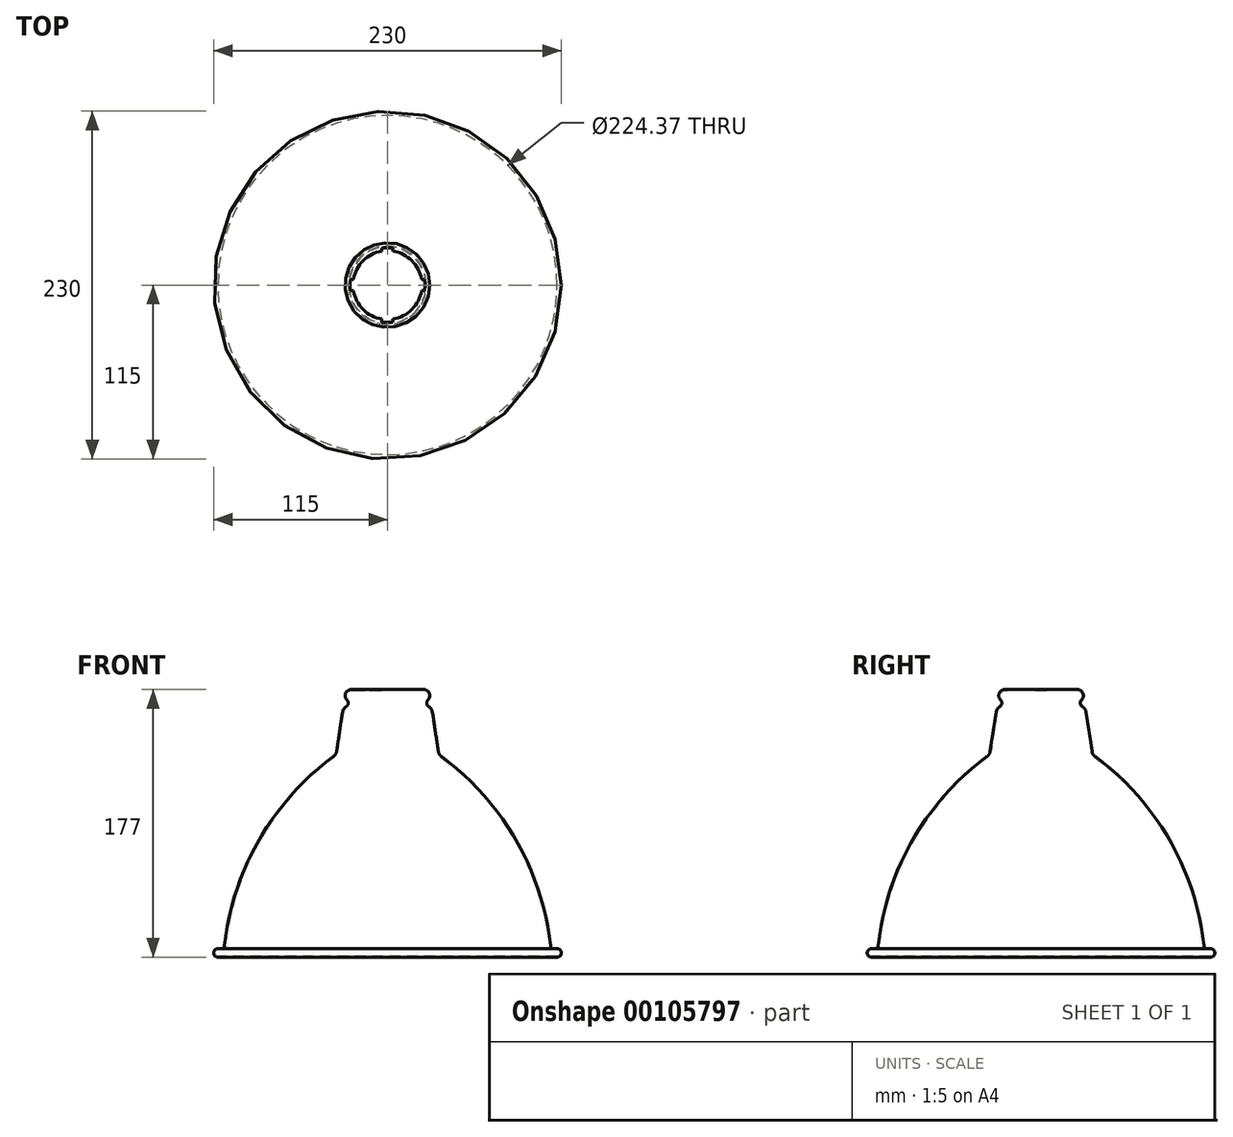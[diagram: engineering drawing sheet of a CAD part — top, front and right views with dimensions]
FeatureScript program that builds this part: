
annotation { "Feature Type Name" : "Feature", "Feature Type Description" : "" }
export const myFeature = defineFeature(function(context is Context, id is Id, definition is map)
    precondition{}
    {
        {
            var Q0;
            Q0=qCreatedBy(makeId("Right.planeOp"),FACE);
            var sketch = newSketch(context, id + "F0", { "sketchPlane" : qUnion([Q0])});
            skLineSegment(sketch, "E0", {"start": v(0, 47.08) * mm, "end": v(0, -149.22) * mm, "construction": true});
            skLineSegment(sketch, "E1", {"start": v(23.94, 47.68) * mm, "end": v(23.94, -145.08) * mm, "construction": true});
            skArc(sketch, "E2", {"start": v(26.81, 37.57) * mm, "mid": v(27.69, 42) * mm, "end": v(23.94, 44.5) * mm});
            skArc(sketch, "E3", {"start": v(26.81, 37.57) * mm, "mid": v(26.02, 35.27) * mm, "end": v(27.34, 33.22) * mm});
            skLineSegment(sketch, "E4", {"start": v(27.15, 46.34) * mm, "end": v(29.2, 32.85) * mm, "construction": true});
            skLineSegment(sketch, "E5", {"start": v(29.69, 29.7) * mm, "end": v(33.69, 3.56) * mm});
            skPoint(sketch, "E6.visualSharp", {"position": v(29.2, 32.85) * mm});
            skArc(sketch, "E6.filletArc", {"start": v(29.69, 29.7) * mm, "mid": v(28.9, 31.73) * mm, "end": v(27.34, 33.22) * mm});
            skPoint(sketch, "E7.visualSharp", {"position": v(34, 1.5) * mm});
            skArc(sketch, "E8", {"start": v(112.19, -132.5) * mm, "mid": v(115, -129.68) * mm, "end": v(112.19, -126.87) * mm});
            skLineSegment(sketch, "E9", {"start": v(112.19, -126.87) * mm, "end": v(109.8, -126.87) * mm});
            skArc(sketch, "E10", {"start": v(107.81, -125.09) * mm, "mid": v(84.89, -54.83) * mm, "end": v(35.66, 0.3) * mm});
            skArc(sketch, "E11.filletArc", {"start": v(33.69, 3.56) * mm, "mid": v(34.35, 1.73) * mm, "end": v(35.66, 0.3) * mm});
            skLineSegment(sketch, "E12", {"start": v(115, -129.68) * mm, "end": v(115, -122.65) * mm, "construction": true});
            skPoint(sketch, "E13.visualSharp", {"position": v(108, -126.87) * mm});
            skArc(sketch, "E13.filletArc", {"start": v(107.81, -125.09) * mm, "mid": v(108.47, -126.36) * mm, "end": v(109.8, -126.87) * mm});
            skArc(sketch, "E14.0", {"start": v(26.46, 37.92) * mm, "mid": v(27.23, 41.8) * mm, "end": v(23.94, 44) * mm});
            skArc(sketch, "E14.1", {"start": v(26.46, 37.92) * mm, "mid": v(25.53, 35.21) * mm, "end": v(27.08, 32.8) * mm});
            skArc(sketch, "E14.2", {"start": v(29.2, 29.63) * mm, "mid": v(28.5, 31.45) * mm, "end": v(27.08, 32.8) * mm});
            skLineSegment(sketch, "E14.3", {"start": v(29.2, 29.63) * mm, "end": v(33.2, 3.49) * mm});
            skArc(sketch, "E14.4", {"start": v(33.2, 3.49) * mm, "mid": v(33.92, 1.48) * mm, "end": v(35.37, -0.1) * mm});
            skArc(sketch, "E14.5", {"start": v(112.19, -132) * mm, "mid": v(114.5, -129.68) * mm, "end": v(112.19, -127.37) * mm});
            skLineSegment(sketch, "E14.6", {"start": v(112.19, -127.37) * mm, "end": v(109.8, -127.37) * mm});
            skArc(sketch, "E14.7", {"start": v(107.32, -125.14) * mm, "mid": v(108.14, -126.73) * mm, "end": v(109.8, -127.37) * mm});
            skArc(sketch, "E14.8", {"start": v(107.32, -125.14) * mm, "mid": v(84.46, -55.08) * mm, "end": v(35.37, -0.1) * mm});
            skLineSegment(sketch, "E15", {"start": v(23.94, 44.5) * mm, "end": v(23.94, 44) * mm});
            skLineSegment(sketch, "E16", {"start": v(112.19, -132) * mm, "end": v(112.19, -132.5) * mm});
            skLineSegment(sketch, "E17", {"start": v(23.94, 44.5) * mm, "end": v(22.8, 44.5) * mm});
            skLineSegment(sketch, "E18", {"start": v(23.94, 44) * mm, "end": v(22.8, 44) * mm});
            skLineSegment(sketch, "E19", {"start": v(22.8, 44) * mm, "end": v(22.8, 44.5) * mm});
            skSolve(sketch);
        }
        {
            var Q0;
            Q0=makeQuery(id+"F0.imprint","IMPRINT",FACE,{"disambiguationData":[TD([[makeQuery(id+"F0.imprint","IMPRINT",EDGE,{"derivedFrom":sQuery(id+"F0.wireOp",EDGE,"E2")}),1.0]])]});
            var Q1;
            Q1=makeQuery(id+"F0.imprint","IMPRINT",FACE,{"disambiguationData":[TD([[makeQuery(id+"F0.imprint","IMPRINT",EDGE,{"derivedFrom":sQuery(id+"F0.wireOp",EDGE,"E15")}),-1.0]])]});
            var Q2;
            Q2=sQuery(id+"F0.wireOp",EDGE,"E0");
            revolve(context, id + "F1", {"entities" : qUnion([Q0, Q1]), "axis" : qUnion([Q2]), "revolveType" : RevolveType.FULL});
        }
        {
            var Q0;
            Q0=makeQuery(id+"F1.opRevolve","SWEPT_FACE",FACE,{"disambiguationData":[OSD([sQuery(id+"F0.wireOp",EDGE,"E17")])]});
            var sketch = newSketch(context, id + "F2", { "sketchPlane" : qUnion([Q0])});
            skLineSegment(sketch, "E20", {"start": v(0, 25.62) * mm, "end": v(0, -27.1) * mm, "construction": true});
            skLineSegment(sketch, "E21", {"start": v(-26.7, 0) * mm, "end": v(26.56, 0) * mm, "construction": true});
            skLineSegment(sketch, "E22", {"start": v(-18.35, 18.35) * mm, "end": v(18.35, -18.35) * mm, "construction": true});
            skCircle(sketch, "E23", {"center": v(0, 0) * mm, "radius": 24.72 * mm});
            skLineSegment(sketch, "E24", {"start": v(-3.65, 22.5) * mm, "end": v(-3.65, 24.45) * mm});
            skLineSegment(sketch, "E25.MirrorCS", {"start": v(3.65, 22.5) * mm, "end": v(3.65, 24.45) * mm});
            skLineSegment(sketch, "E26.MirrorCS", {"start": v(-3.65, -22.5) * mm, "end": v(-3.65, -24.45) * mm});
            skLineSegment(sketch, "E27.MirrorCS", {"start": v(3.65, -22.5) * mm, "end": v(3.65, -24.45) * mm});
            skLineSegment(sketch, "E28.MirrorCS", {"start": v(-22.5, 3.65) * mm, "end": v(-24.45, 3.65) * mm});
            skLineSegment(sketch, "E29.MirrorCS", {"start": v(-22.5, -3.65) * mm, "end": v(-24.45, -3.65) * mm});
            skLineSegment(sketch, "E30.MirrorCS", {"start": v(22.5, -3.65) * mm, "end": v(24.45, -3.65) * mm});
            skLineSegment(sketch, "E31.MirrorCS", {"start": v(22.5, 3.65) * mm, "end": v(24.45, 3.65) * mm});
            skSolve(sketch);
        }
        {
            var Q0;
            {var subQ0=sQuery(id+"F2.wireOp",EDGE,"E28.MirrorCS");var subQ1=sQuery(id+"F0.wireOp",EDGE,"E17");var subQ2=makeQuery(id+"F1.opRevolve","SWEPT_EDGE",EDGE,{"disambiguationData":[OSD([subQ1,sQuery(id+"F0.wireOp",EDGE,"E19")])]});var subQ3=makeQuery(id+"F2.imprint","INTERSECT",VERTEX,{"derivedFrom":[subQ2,subQ0]});Q0=makeQuery(id+"F2.imprint","IMPRINT",FACE,{"disambiguationData":[TD([[makeQuery(id+"F2.imprint","IMPRINT",EDGE,{"disambiguationData":[TD([[subQ3,-1.0]])],"derivedFrom":subQ0}),1.0]])]});}
            var Q1;
            {var subQ0=sQuery(id+"F2.wireOp",EDGE,"E28.MirrorCS");var subQ1=sQuery(id+"F2.wireOp",EDGE,"E23");var subQ2=makeQuery(id+"F2.imprint","INTERSECT",VERTEX,{"derivedFrom":[subQ1,subQ0]});Q1=makeQuery(id+"F2.imprint","IMPRINT",FACE,{"disambiguationData":[TD([[makeQuery(id+"F2.imprint","IMPRINT",EDGE,{"disambiguationData":[TD([[subQ2,-1.0]])],"derivedFrom":subQ1}),1.0]])]});}
            var Q2;
            {var subQ0=sQuery(id+"F2.wireOp",EDGE,"E24");var subQ1=sQuery(id+"F0.wireOp",EDGE,"E17");var subQ2=makeQuery(id+"F1.opRevolve","SWEPT_EDGE",EDGE,{"disambiguationData":[OSD([subQ1,sQuery(id+"F0.wireOp",EDGE,"E19")])]});var subQ3=makeQuery(id+"F2.imprint","INTERSECT",VERTEX,{"derivedFrom":[subQ2,subQ0]});Q2=makeQuery(id+"F2.imprint","IMPRINT",FACE,{"disambiguationData":[TD([[makeQuery(id+"F2.imprint","IMPRINT",EDGE,{"disambiguationData":[TD([[subQ3,-1.0]])],"derivedFrom":subQ0}),-1.0]])]});}
            var Q3;
            {var subQ0=sQuery(id+"F2.wireOp",EDGE,"E24");var subQ1=sQuery(id+"F2.wireOp",EDGE,"E23");var subQ2=makeQuery(id+"F2.imprint","INTERSECT",VERTEX,{"derivedFrom":[subQ1,subQ0]});Q3=makeQuery(id+"F2.imprint","IMPRINT",FACE,{"disambiguationData":[TD([[makeQuery(id+"F2.imprint","IMPRINT",EDGE,{"disambiguationData":[TD([[subQ2,1.0]])],"derivedFrom":subQ1}),1.0]])]});}
            var Q4;
            {var subQ0=sQuery(id+"F2.wireOp",EDGE,"E30.MirrorCS");var subQ1=sQuery(id+"F0.wireOp",EDGE,"E17");var subQ2=makeQuery(id+"F1.opRevolve","SWEPT_EDGE",EDGE,{"disambiguationData":[OSD([subQ1,sQuery(id+"F0.wireOp",EDGE,"E19")])]});var subQ3=makeQuery(id+"F2.imprint","INTERSECT",VERTEX,{"derivedFrom":[subQ2,subQ0]});Q4=makeQuery(id+"F2.imprint","IMPRINT",FACE,{"disambiguationData":[TD([[makeQuery(id+"F2.imprint","IMPRINT",EDGE,{"disambiguationData":[TD([[subQ3,-1.0]])],"derivedFrom":subQ0}),1.0]])]});}
            var Q5;
            {var subQ0=sQuery(id+"F2.wireOp",EDGE,"E30.MirrorCS");var subQ1=sQuery(id+"F2.wireOp",EDGE,"E23");var subQ2=makeQuery(id+"F2.imprint","INTERSECT",VERTEX,{"derivedFrom":[subQ1,subQ0]});Q5=makeQuery(id+"F2.imprint","IMPRINT",FACE,{"disambiguationData":[TD([[makeQuery(id+"F2.imprint","IMPRINT",EDGE,{"disambiguationData":[TD([[subQ2,-1.0]])],"derivedFrom":subQ1}),1.0]])]});}
            var Q6;
            {var subQ0=sQuery(id+"F2.wireOp",EDGE,"E26.MirrorCS");var subQ1=sQuery(id+"F0.wireOp",EDGE,"E17");var subQ2=makeQuery(id+"F1.opRevolve","SWEPT_EDGE",EDGE,{"disambiguationData":[OSD([subQ1,sQuery(id+"F0.wireOp",EDGE,"E19")])]});var subQ3=makeQuery(id+"F2.imprint","INTERSECT",VERTEX,{"derivedFrom":[subQ2,subQ0]});Q6=makeQuery(id+"F2.imprint","IMPRINT",FACE,{"disambiguationData":[TD([[makeQuery(id+"F2.imprint","IMPRINT",EDGE,{"disambiguationData":[TD([[subQ3,-1.0]])],"derivedFrom":subQ0}),1.0]])]});}
            var Q7;
            {var subQ0=sQuery(id+"F2.wireOp",EDGE,"E26.MirrorCS");var subQ1=sQuery(id+"F2.wireOp",EDGE,"E23");var subQ2=makeQuery(id+"F2.imprint","INTERSECT",VERTEX,{"derivedFrom":[subQ1,subQ0]});Q7=makeQuery(id+"F2.imprint","IMPRINT",FACE,{"disambiguationData":[TD([[makeQuery(id+"F2.imprint","IMPRINT",EDGE,{"disambiguationData":[TD([[subQ2,-1.0]])],"derivedFrom":subQ1}),1.0]])]});}
            extrude(context, id + "F3", {"entities" : qUnion([Q0, Q1, Q2, Q3, Q4, Q5, Q6, Q7]), "operationType" : NewBodyOperationType.REMOVE, "endBound" : BoundingType.THROUGH_ALL, "oppositeDirection" : true, "depth" : 25 * mm});
        }
    });
